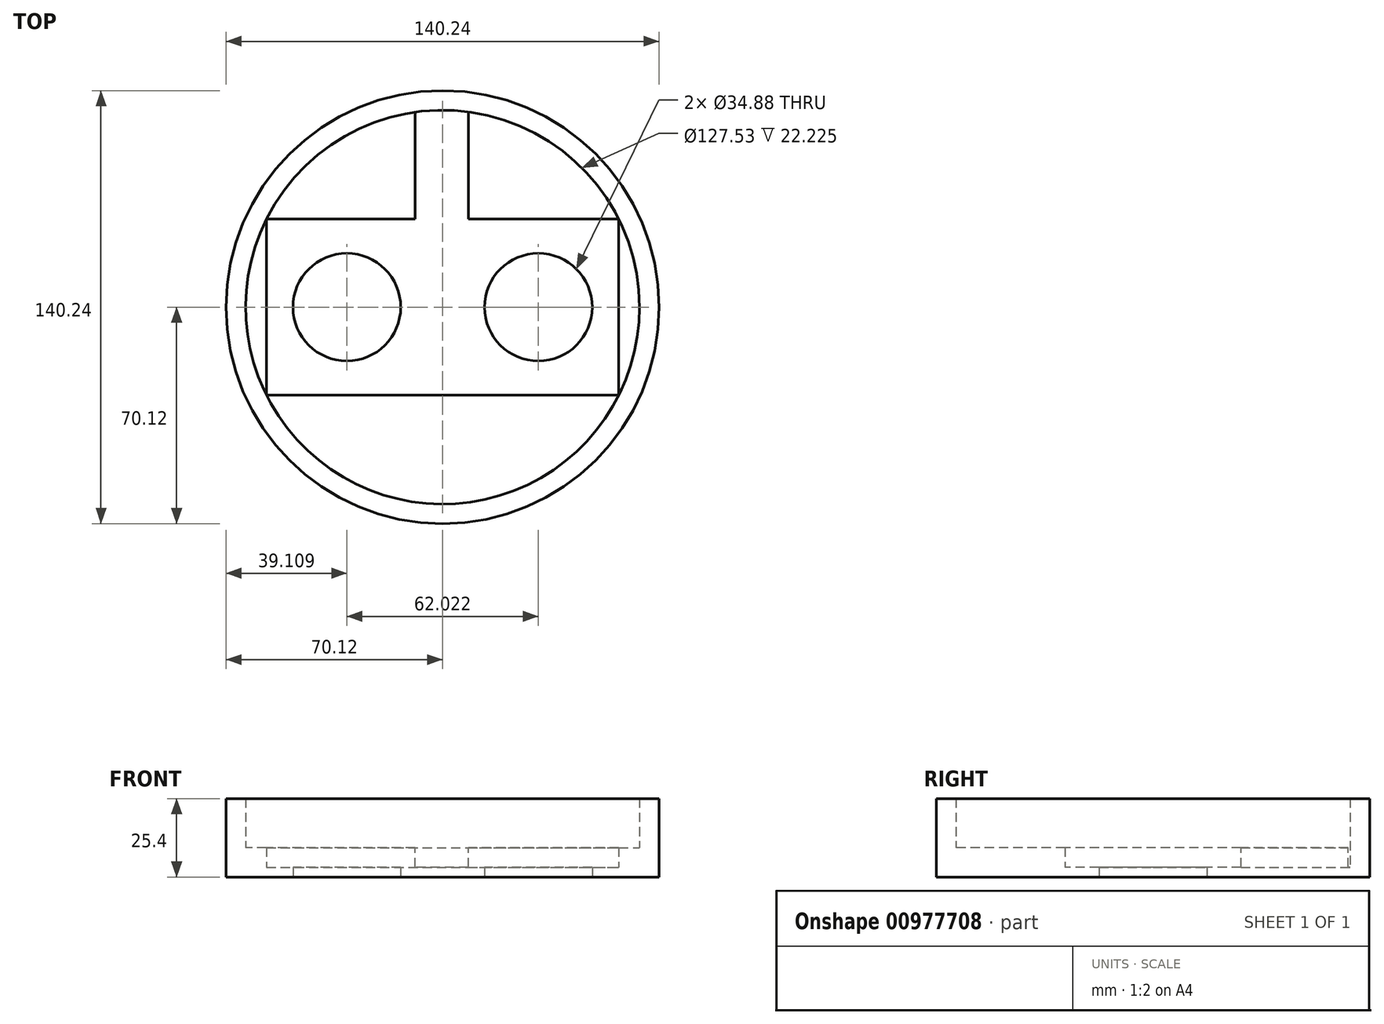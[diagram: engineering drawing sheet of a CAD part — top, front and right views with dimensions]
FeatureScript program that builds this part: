
annotation { "Feature Type Name" : "Feature", "Feature Type Description" : "" }
export const myFeature = defineFeature(function(context is Context, id is Id, definition is map)
    precondition{}
    {
        {
            var Q0;
            Q0=qCreatedBy(makeId("Top.planeOp"),FACE);
            var sketch = newSketch(context, id + "F0", { "sketchPlane" : qUnion([Q0])});
            skCircle(sketch, "E0", {"center": v(0, 0) * mm, "radius": 63.77 * mm});
            skLineSegment(sketch, "E1.bottom", {"start": v(-57.05, 28.49) * mm, "end": v(57.05, 28.49) * mm});
            skLineSegment(sketch, "E1.top", {"start": v(-57.05, -28.49) * mm, "end": v(57.05, -28.49) * mm});
            skLineSegment(sketch, "E1.left", {"start": v(-57.05, 28.49) * mm, "end": v(-57.05, -28.49) * mm});
            skLineSegment(sketch, "E1.right", {"start": v(57.05, 28.49) * mm, "end": v(57.05, -28.49) * mm});
            skCircle(sketch, "E2", {"center": v(-31.01, 0) * mm, "radius": 17.44 * mm});
            skCircle(sketch, "E3.MirrorC", {"center": v(31.01, 0) * mm, "radius": 17.44 * mm});
            skCircle(sketch, "E4.0", {"center": v(0, 0) * mm, "radius": 70.12 * mm});
            skSolve(sketch);
        }
        {
            var Q0;
            Q0=makeQuery(id+"F0.imprint","IMPRINT",FACE,{"disambiguationData":[TD([[makeQuery(id+"F0.imprint","IMPRINT",EDGE,{"derivedFrom":sQuery(id+"F0.wireOp",EDGE,"E4.0")}),1.0]])]});
            extrude(context, id + "F1", {"entities" : qUnion([Q0]), "depth" : 25.4 * mm, "offsetDistance" : 25.4 * mm});
        }
        {
            var Q0;
            {var subQ0=sQuery(id+"F0.wireOp",EDGE,"E1.bottom");Q0=makeQuery(id+"F0.imprint","IMPRINT",FACE,{"disambiguationData":[TD([[makeQuery(id+"F0.imprint","IMPRINT",EDGE,{"derivedFrom":subQ0}),1.0]])]});}
            var Q1;
            {var subQ0=sQuery(id+"F0.wireOp",EDGE,"E1.left");Q1=makeQuery(id+"F0.imprint","IMPRINT",FACE,{"disambiguationData":[TD([[makeQuery(id+"F0.imprint","IMPRINT",EDGE,{"derivedFrom":subQ0}),-1.0]])]});}
            var Q2;
            {var subQ0=sQuery(id+"F0.wireOp",EDGE,"E1.top");Q2=makeQuery(id+"F0.imprint","IMPRINT",FACE,{"disambiguationData":[TD([[makeQuery(id+"F0.imprint","IMPRINT",EDGE,{"derivedFrom":subQ0}),-1.0]])]});}
            var Q3;
            {var subQ0=sQuery(id+"F0.wireOp",EDGE,"E1.right");Q3=makeQuery(id+"F0.imprint","IMPRINT",FACE,{"disambiguationData":[TD([[makeQuery(id+"F0.imprint","IMPRINT",EDGE,{"derivedFrom":subQ0}),1.0]])]});}
            extrude(context, id + "F2", {"entities" : qUnion([Q0, Q1, Q2, Q3]), "operationType" : NewBodyOperationType.ADD, "depth" : 9.52 * mm, "offsetDistance" : 25.4 * mm});
        }
        {
            var Q0;
            Q0=makeQuery(id+"F0.imprint","IMPRINT",FACE,{"disambiguationData":[TD([[makeQuery(id+"F0.imprint","IMPRINT",EDGE,{"derivedFrom":sQuery(id+"F0.wireOp",EDGE,"E1.bottom")}),-1.0]])]});
            extrude(context, id + "F3", {"entities" : qUnion([Q0]), "operationType" : NewBodyOperationType.ADD, "depth" : 3.17 * mm, "offsetDistance" : 25.4 * mm});
        }
        {
            var Q0;
            Q0=makeQuery(id+"F2.opExtrude","CAP_FACE",FACE,{"disambiguationData":[OSD([sQuery(id+"F0.wireOp",EDGE,"E0"),sQuery(id+"F0.wireOp",EDGE,"E1.bottom")])],"isStart":false});
            var sketch = newSketch(context, id + "F4", { "sketchPlane" : qUnion([Q0])});
            skLineSegment(sketch, "E5.bottom", {"start": v(-8.9, 28.49) * mm, "end": v(8.3, 28.49) * mm});
            skLineSegment(sketch, "E5.left", {"start": v(-8.9, 28.49) * mm, "end": v(-8.9, 63.22) * mm});
            skLineSegment(sketch, "E5.right", {"start": v(8.3, 28.49) * mm, "end": v(8.3, 63.22) * mm});
            skSolve(sketch);
        }
        {
            var Q0;
            {var subQ0=sQuery(id+"F4.wireOp",EDGE,"E5.bottom");Q0=makeQuery(id+"F4.imprint","IMPRINT",FACE,{"disambiguationData":[TD([[makeQuery(id+"F4.imprint","IMPRINT",EDGE,{"derivedFrom":subQ0}),1.0]])]});}
            extrude(context, id + "F5", {"entities" : qUnion([Q0]), "operationType" : NewBodyOperationType.REMOVE, "oppositeDirection" : true, "depth" : 6.35 * mm, "offsetDistance" : 25.4 * mm});
        }
    });
